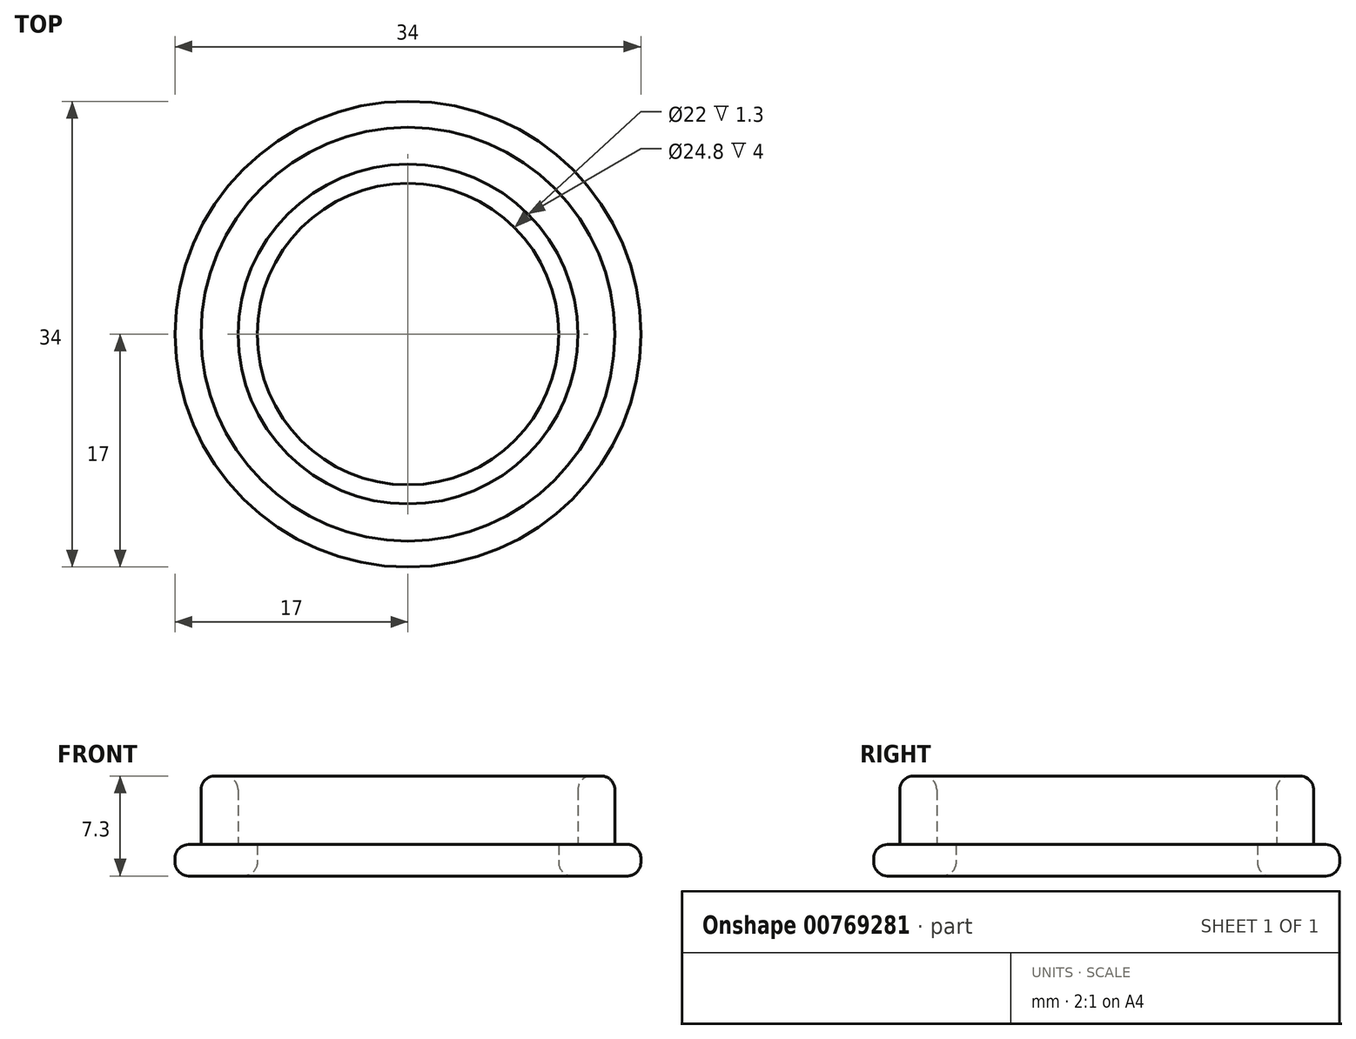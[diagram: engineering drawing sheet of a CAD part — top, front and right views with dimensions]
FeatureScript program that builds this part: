
annotation { "Feature Type Name" : "Feature", "Feature Type Description" : "" }
export const myFeature = defineFeature(function(context is Context, id is Id, definition is map)
    precondition{}
    {
        {
            var Q0;
            Q0=qCreatedBy(makeId("Top.planeOp"),FACE);
            var sketch = newSketch(context, id + "F0", { "sketchPlane" : qUnion([Q0])});
            skCircle(sketch, "E0", {"center": v(0, 0) * mm, "radius": 17 * mm});
            skCircle(sketch, "E1", {"center": v(0, 0) * mm, "radius": 11 * mm});
            skSolve(sketch);
        }
        {
            var Q0;
            Q0=makeQuery(id+"F0.imprint","IMPRINT",FACE,{"disambiguationData":[TD([[makeQuery(id+"F0.imprint","IMPRINT",EDGE,{"derivedFrom":sQuery(id+"F0.wireOp",EDGE,"E0")}),1.0]])]});
            extrude(context, id + "F1", {"entities" : qUnion([Q0]), "depth" : 2.3 * mm, "offsetDistance" : 25.4 * mm});
        }
        {
            var Q0;
            Q0=makeQuery(id+"F1.opExtrude","CAP_FACE",FACE,{"disambiguationData":[OSD([sQuery(id+"F0.wireOp",EDGE,"E0"),sQuery(id+"F0.wireOp",EDGE,"E1")])],"isStart":false});
            var sketch = newSketch(context, id + "F2", { "sketchPlane" : qUnion([Q0])});
            skCircle(sketch, "E2", {"center": v(0, 0) * mm, "radius": 12.4 * mm});
            skCircle(sketch, "E3", {"center": v(0, 0) * mm, "radius": 15.1 * mm});
            skSolve(sketch);
        }
        {
            var Q0;
            Q0=makeQuery(id+"F2.imprint","IMPRINT",FACE,{"disambiguationData":[TD([[makeQuery(id+"F2.imprint","IMPRINT",EDGE,{"derivedFrom":sQuery(id+"F2.wireOp",EDGE,"E2")}),-1.0]])]});
            extrude(context, id + "F3", {"entities" : qUnion([Q0]), "operationType" : NewBodyOperationType.ADD, "depth" : 5 * mm, "offsetDistance" : 25 * mm});
        }
        {
            var Q0;
            Q0=makeQuery(id+"F1.opExtrude","CAP_EDGE",EDGE,{"disambiguationData":[OSD([sQuery(id+"F0.wireOp",EDGE,"E0")])],"isStart":true});
            var Q1;
            Q1=makeQuery(id+"F1.opExtrude","CAP_EDGE",EDGE,{"disambiguationData":[OSD([sQuery(id+"F0.wireOp",EDGE,"E1")])],"isStart":true});
            var Q2;
            Q2=makeQuery(id+"F3.opExtrude","CAP_EDGE",EDGE,{"disambiguationData":[OSD([sQuery(id+"F2.wireOp",EDGE,"E3")])],"isStart":false});
            var Q3;
            Q3=makeQuery(id+"F3.opExtrude","CAP_EDGE",EDGE,{"disambiguationData":[OSD([sQuery(id+"F2.wireOp",EDGE,"E2")])],"isStart":false});
            var Q4;
            Q4=makeQuery(id+"F1.opExtrude","CAP_EDGE",EDGE,{"disambiguationData":[OSD([sQuery(id+"F0.wireOp",EDGE,"E0")])],"isStart":false});
            fillet(context, id + "F4", {"entities" : qUnion([Q0, Q1, Q2, Q3, Q4]), "radius" : 1 * mm, "tangentPropagation" : true, "allowEdgeOverflow" : false});
        }
    });
